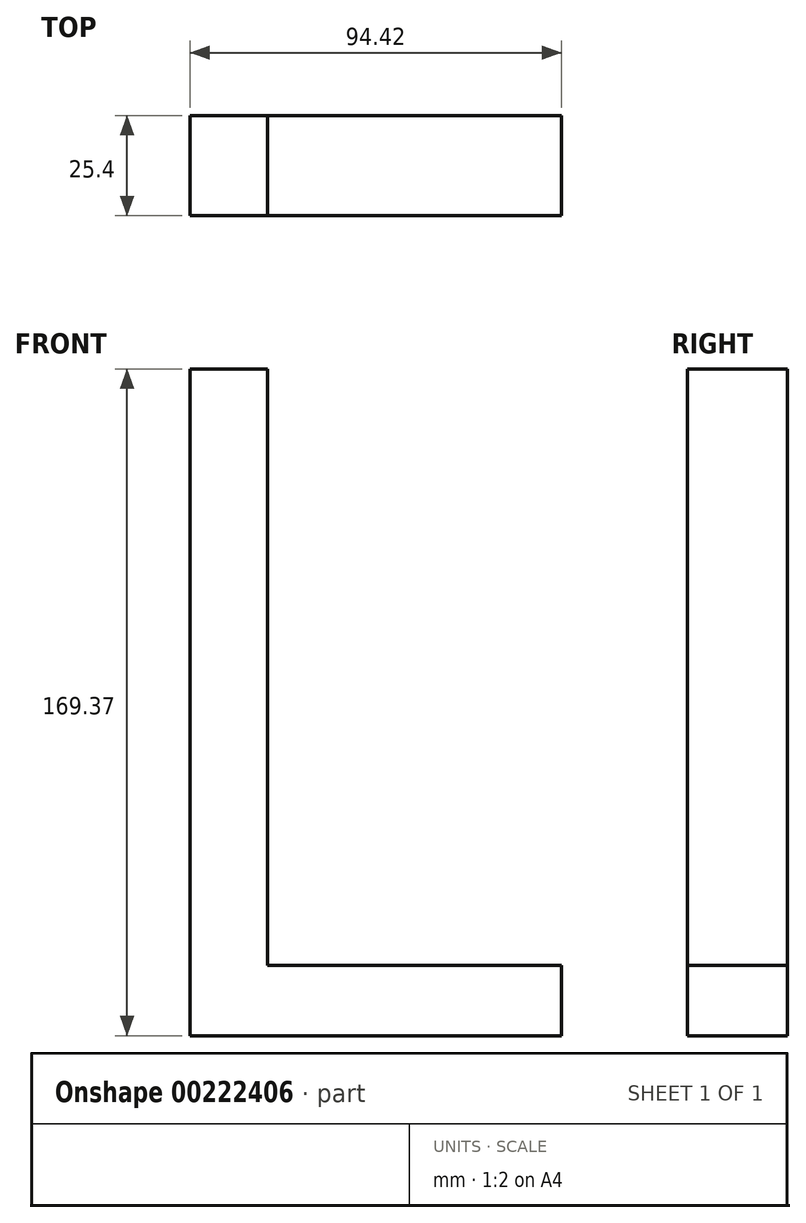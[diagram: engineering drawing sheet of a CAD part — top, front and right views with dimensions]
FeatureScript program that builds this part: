
annotation { "Feature Type Name" : "Feature", "Feature Type Description" : "" }
export const myFeature = defineFeature(function(context is Context, id is Id, definition is map)
    precondition{}
    {
        {
            var Q0;
            Q0=qCreatedBy(makeId("Front.planeOp"),FACE);
            var sketch = newSketch(context, id + "F0", { "sketchPlane" : qUnion([Q0])});
            skText(sketch, "E0", { "text": "L", "fontName": "OpenSans-Regular.ttf"});
            const initialGuessF0  = {"E0": [-0.07755, -0.08605, 1, 0, 0.17082]};
            skSetInitialGuess(sketch, initialGuessF0);
            skSolve(sketch);
        }
        {
            var Q0;
            Q0 = qSketchRegion(id + "F0", true);
            extrude(context, id + "F1", {"entities" : qUnion([Q0]), "oppositeDirection" : true, "depth" : 25.4 * mm});
        }
    });
